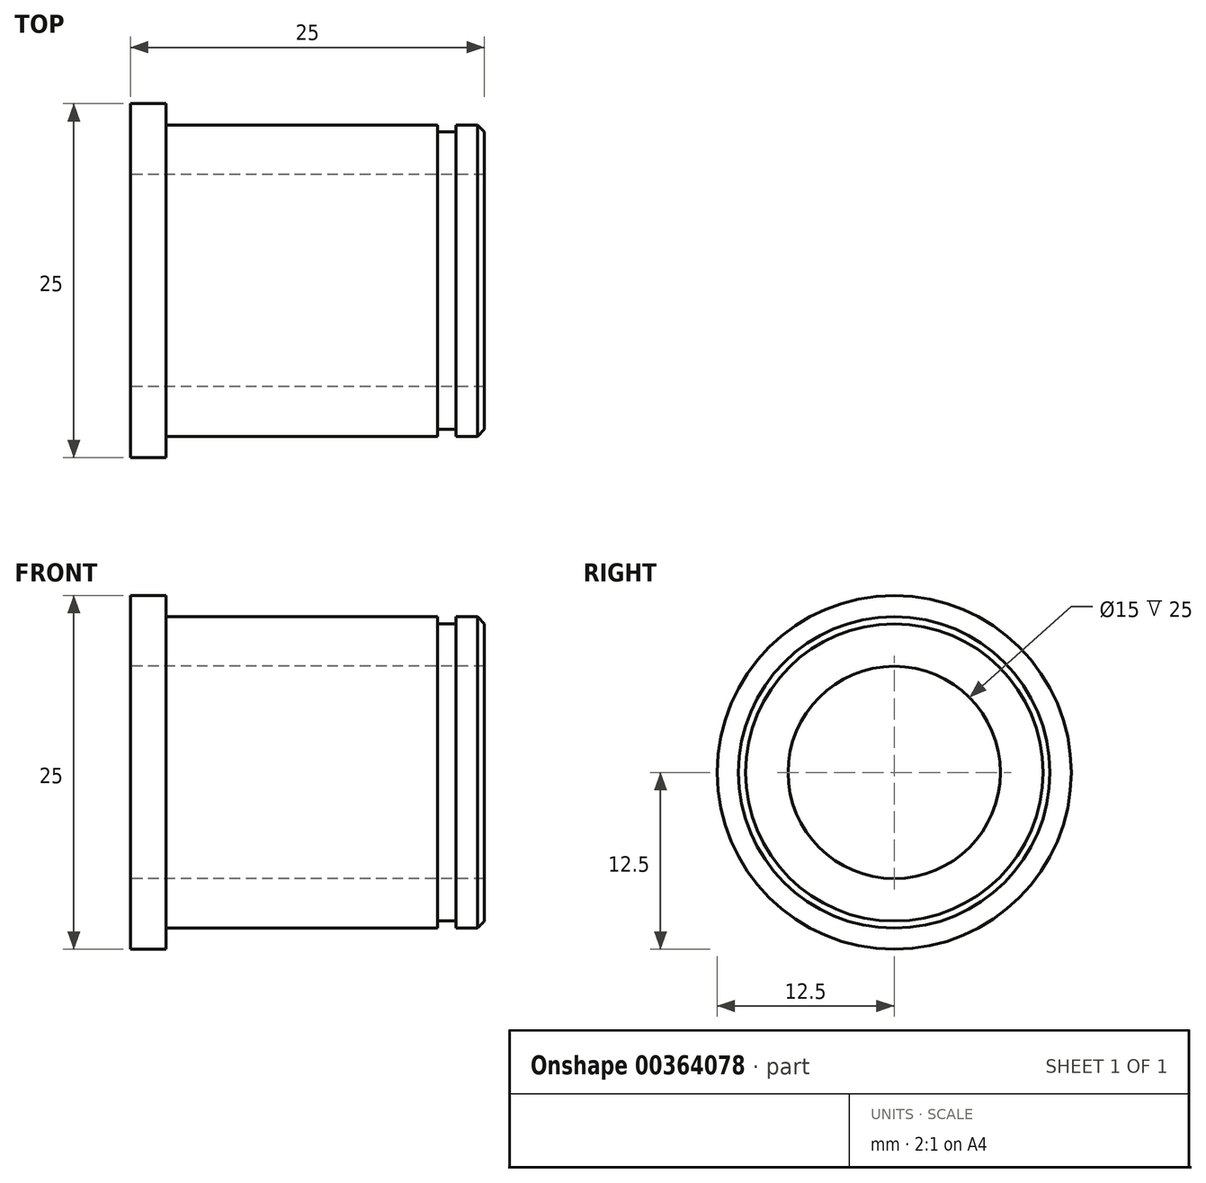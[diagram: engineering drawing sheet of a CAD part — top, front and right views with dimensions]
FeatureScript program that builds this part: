
annotation { "Feature Type Name" : "Feature", "Feature Type Description" : "" }
export const myFeature = defineFeature(function(context is Context, id is Id, definition is map)
    precondition{}
    {
        {
            var Q0;
            Q0=qCreatedBy(makeId("Top.planeOp"),FACE);
            var sketch = newSketch(context, id + "F0", { "sketchPlane" : qUnion([Q0])});
            skLineSegment(sketch, "E0", {"start": v(0, 0) * mm, "end": v(12.9, 0) * mm, "construction": true});
            skLineSegment(sketch, "E1", {"start": v(0, 7.5) * mm, "end": v(0, 12.5) * mm});
            skLineSegment(sketch, "E2", {"start": v(0, 12.5) * mm, "end": v(2.5, 12.5) * mm});
            skLineSegment(sketch, "E3", {"start": v(2.5, 12.5) * mm, "end": v(2.5, 11) * mm});
            skLineSegment(sketch, "E4", {"start": v(2.5, 11) * mm, "end": v(25, 11) * mm});
            skLineSegment(sketch, "E5", {"start": v(25, 11) * mm, "end": v(25, 7.5) * mm});
            skLineSegment(sketch, "E6", {"start": v(25, 7.5) * mm, "end": v(0, 7.5) * mm});
            skSolve(sketch);
        }
        {
            var Q0;
            Q0=makeQuery(id+"F0.imprint","IMPRINT",FACE,{"disambiguationData":[TD([[makeQuery(id+"F0.imprint","IMPRINT",EDGE,{"derivedFrom":sQuery(id+"F0.wireOp",EDGE,"E1")}),-1.0]])]});
            var Q1;
            Q1=sQuery(id+"F0.wireOp",EDGE,"E0");
            revolve(context, id + "F1", {"entities" : qUnion([Q0]), "axis" : qUnion([Q1]), "revolveType" : RevolveType.FULL});
        }
        {
            var Q0;
            Q0=makeQuery(id+"F1.opRevolve","SWEPT_EDGE",EDGE,{"disambiguationData":[OSD([sQuery(id+"F0.wireOp",EDGE,"E4"),sQuery(id+"F0.wireOp",EDGE,"E5")])]});
            chamfer(context, id + "F2", {"entities" : qUnion([Q0]), "width" : 0.5 * mm, "tangentPropagation" : true});
        }
        {
            var Q0;
            Q0=qCreatedBy(makeId("Front.planeOp"),FACE);
            var sketch = newSketch(context, id + "F3", { "sketchPlane" : qUnion([Q0])});
            skLineSegment(sketch, "E7.bottom", {"start": v(21.7, 11) * mm, "end": v(23, 11) * mm});
            skLineSegment(sketch, "E7.top", {"start": v(21.7, 10.5) * mm, "end": v(23, 10.5) * mm});
            skLineSegment(sketch, "E7.left", {"start": v(21.7, 11) * mm, "end": v(21.7, 10.5) * mm});
            skLineSegment(sketch, "E7.right", {"start": v(23, 11) * mm, "end": v(23, 10.5) * mm});
            skLineSegment(sketch, "E8", {"start": v(0, 0) * mm, "end": v(31.69, 0) * mm, "construction": true});
            skLineSegment(sketch, "E9", {"start": v(2.5, -11) * mm, "end": v(24.5, -11) * mm});
            skLineSegment(sketch, "E10", {"start": v(24.5, 11) * mm, "end": v(2.5, 11) * mm});
            skSolve(sketch);
        }
        {
            var Q0;
            Q0=makeQuery(id+"F3.imprint","IMPRINT",FACE,{"disambiguationData":[TD([[makeQuery(id+"F3.imprint","IMPRINT",EDGE,{"derivedFrom":sQuery(id+"F3.wireOp",EDGE,"E7.top")}),1.0]])]});
            var Q1;
            Q1=sQuery(id+"F3.wireOp",EDGE,"E8");
            revolve(context, id + "F4", {"operationType" : NewBodyOperationType.REMOVE, "entities" : qUnion([Q0]), "axis" : qUnion([Q1]), "revolveType" : RevolveType.FULL, "oppositeDirection" : true});
        }
    });
